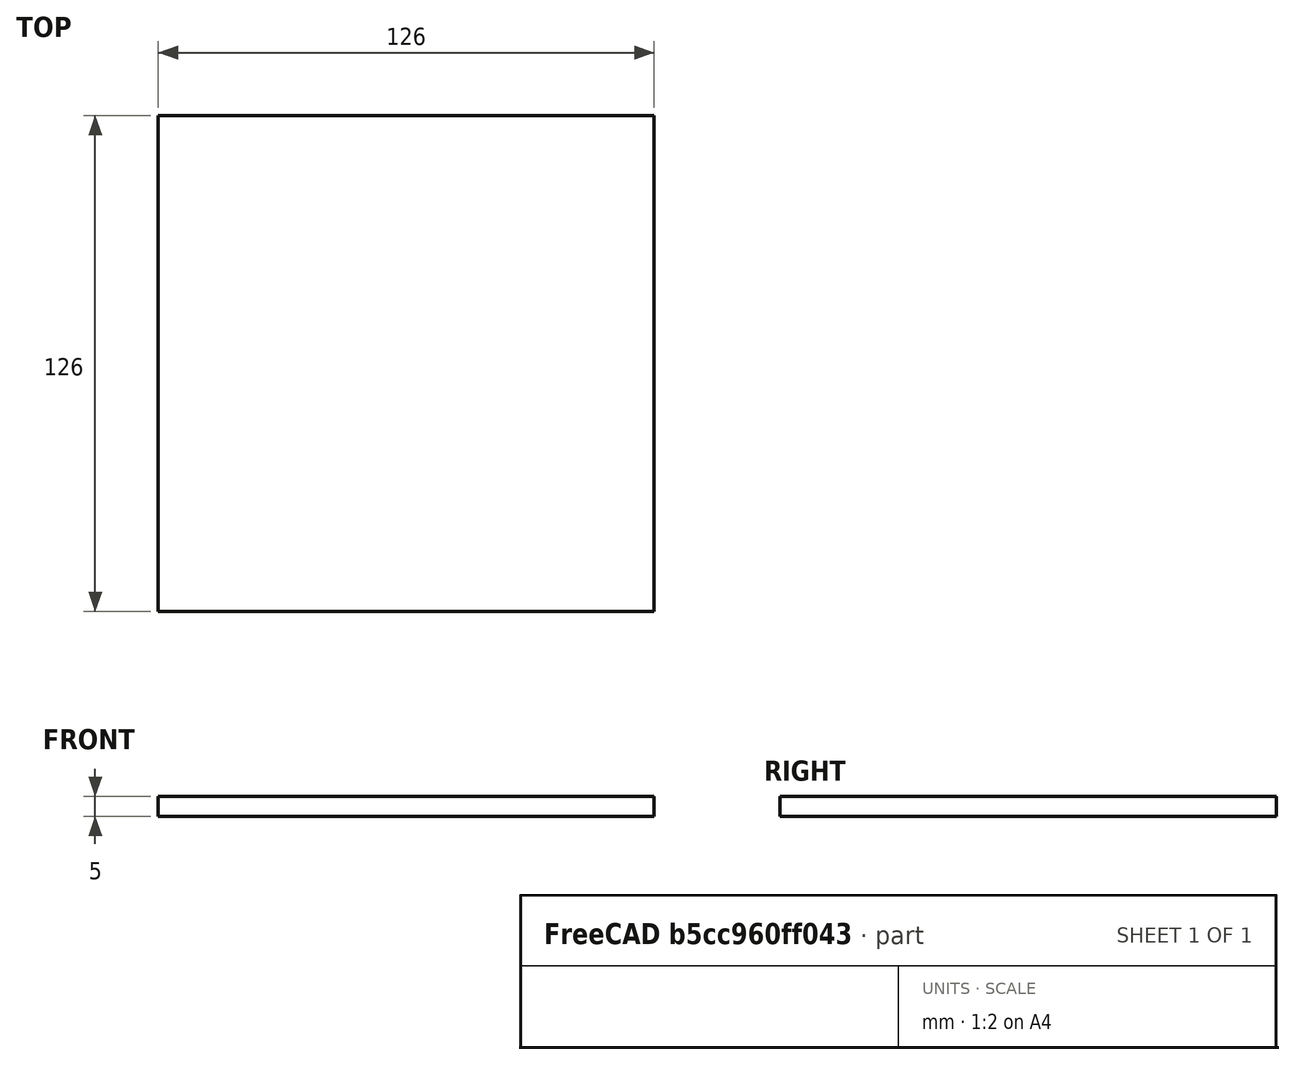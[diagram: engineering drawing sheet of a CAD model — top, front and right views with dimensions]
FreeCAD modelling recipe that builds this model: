
FCSTD DOCUMENT  (FreeCAD 1.0R39319 (Git))
Label: chapa_retangular_126x126x5
License: All rights reserved
LicenseURL: https://en.wikipedia.org/wiki/All_rights_reserved
objects: Sketcher::SketchObject×1, PartDesign::Pad×1, PartDesign::Body×1
note: 6 computed .brp shape members not serialized (recipe doc carries the construction recipe); baked Part::Feature solids carry a one-line shape summary decoded from their .brp

FEATURE [Sketcher::SketchObject] Sketch_1
  ArcFitTolerance = 1e-06
  AttachmentSupport = -> [XY_Plane]
  FullyConstrained = false
  MakeInternals = false
  MapMode = 5
  sketch-geometry (4):
    g0: LineSegment StartX=-63 StartY=-63 StartZ=0 EndX=63 EndY=-63 EndZ=0
    g1: LineSegment StartX=63 StartY=-63 StartZ=0 EndX=63 EndY=63 EndZ=0
    g2: LineSegment StartX=63 StartY=63 StartZ=0 EndX=-63 EndY=63 EndZ=0
    g3: LineSegment StartX=-63 StartY=63 StartZ=0 EndX=-63 EndY=-63 EndZ=0
  constraints (4):
    c: Coincident(g0,g1)
    c: Coincident(g1,g2)
    c: Coincident(g2,g3)
    c: Coincident(g3,g0)
FEATURE [PartDesign::Pad] Pad_1
  Direction = (0,0,1)
  Length = 5
  Length2 = 10
  Profile = -> Sketch_1
  Refine = true
  Suppressed = false
  Type = 0
FEATURE [PartDesign::Body] Body
  AllowCompound = false
  Group = -> [Sketch_1,Pad_1]
  Origin = -> Origin
  Tip = -> Pad_1
